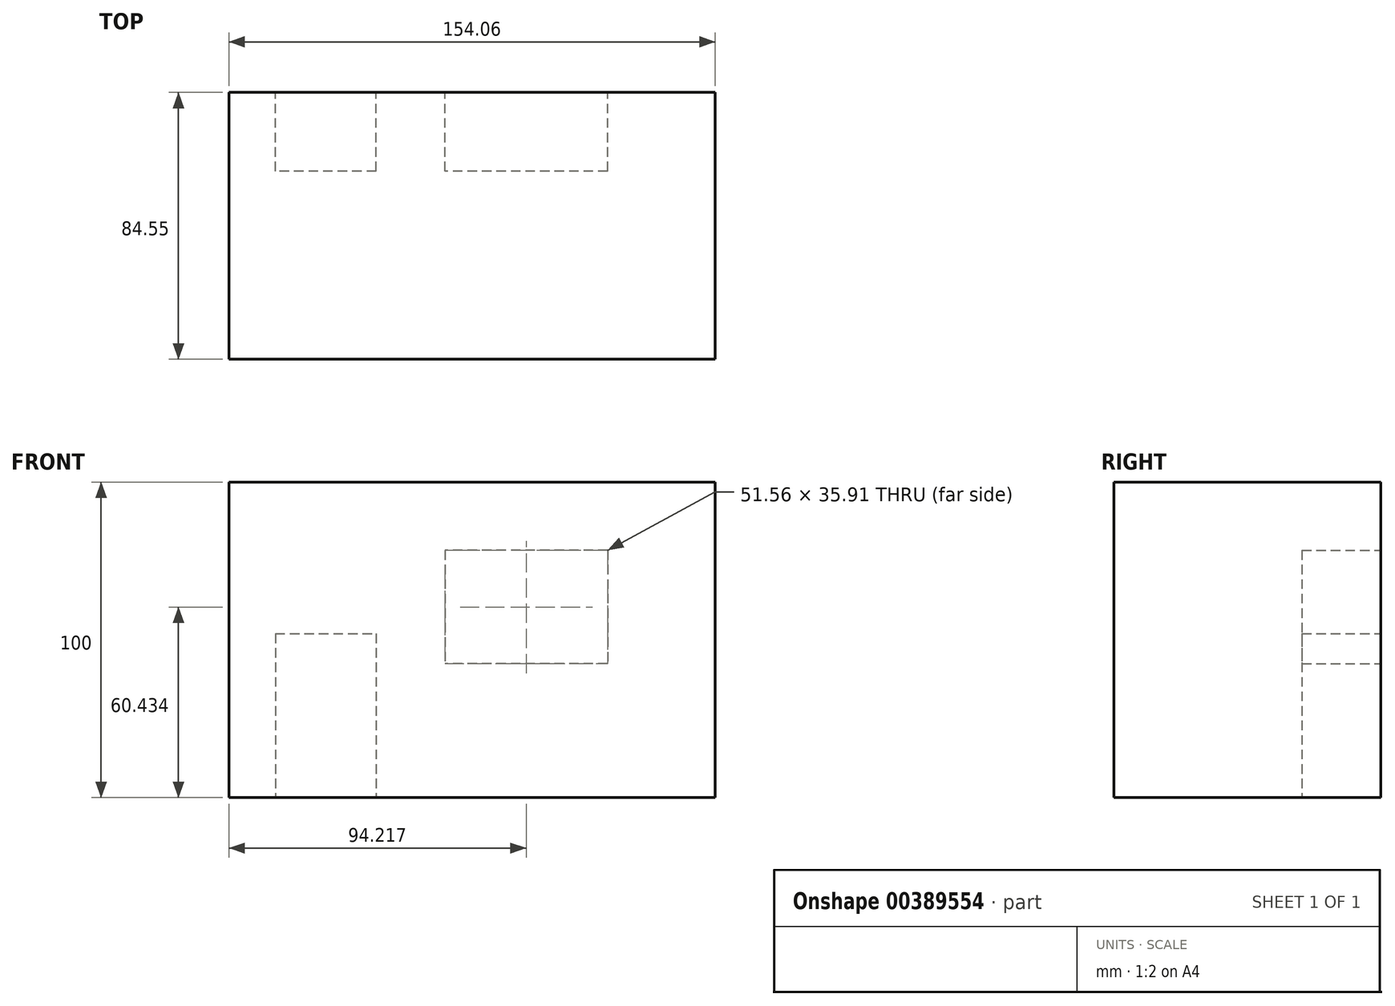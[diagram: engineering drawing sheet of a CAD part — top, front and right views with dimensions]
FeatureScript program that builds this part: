
annotation { "Feature Type Name" : "Feature", "Feature Type Description" : "" }
export const myFeature = defineFeature(function(context is Context, id is Id, definition is map)
    precondition{}
    {
        {
            var Q0;
            Q0=qCreatedBy(makeId("Top.planeOp"),FACE);
            var sketch = newSketch(context, id + "F0", { "sketchPlane" : qUnion([Q0])});
            skLineSegment(sketch, "E0.bottom", {"start": v(0, 0) * mm, "end": v(-154.06, 0) * mm});
            skLineSegment(sketch, "E0.top", {"start": v(0, -84.55) * mm, "end": v(-154.06, -84.55) * mm});
            skLineSegment(sketch, "E0.left", {"start": v(0, 0) * mm, "end": v(0, -84.55) * mm});
            skLineSegment(sketch, "E0.right", {"start": v(-154.06, 0) * mm, "end": v(-154.06, -84.55) * mm});
            skSolve(sketch);
        }
        {
            var Q0;
            Q0=makeQuery(id+"F0.imprint","IMPRINT",FACE,{"disambiguationData":[TD([[makeQuery(id+"F0.imprint","IMPRINT",EDGE,{"derivedFrom":sQuery(id+"F0.wireOp",EDGE,"E0.bottom")}),1.0]])]});
            extrude(context, id + "F1", {"entities" : qUnion([Q0]), "depth" : 100 * mm});
        }
        {
            var Q0;
            Q0=makeQuery(id+"F1.opExtrude","SWEPT_FACE",FACE,{"disambiguationData":[OSD([sQuery(id+"F0.wireOp",EDGE,"E0.bottom")])]});
            var sketch = newSketch(context, id + "F2", { "sketchPlane" : qUnion([Q0])});
            skLineSegment(sketch, "E1.bottom", {"start": v(34.06, 78.39) * mm, "end": v(85.62, 78.39) * mm});
            skLineSegment(sketch, "E1.top", {"start": v(34.06, 42.48) * mm, "end": v(85.62, 42.48) * mm});
            skLineSegment(sketch, "E1.left", {"start": v(34.06, 78.39) * mm, "end": v(34.06, 42.48) * mm});
            skLineSegment(sketch, "E1.right", {"start": v(85.62, 78.39) * mm, "end": v(85.62, 42.48) * mm});
            skLineSegment(sketch, "E2.bottom", {"start": v(139.33, 52) * mm, "end": v(107.4, 52) * mm});
            skLineSegment(sketch, "E2.top", {"start": v(139.33, -23.2) * mm, "end": v(107.4, -23.2) * mm});
            skLineSegment(sketch, "E2.left", {"start": v(139.33, 52) * mm, "end": v(139.33, -23.2) * mm});
            skLineSegment(sketch, "E2.right", {"start": v(107.4, 52) * mm, "end": v(107.4, -23.2) * mm});
            skSolve(sketch);
        }
        {
            var Q0;
            {var subQ0=sQuery(id+"F2.wireOp",EDGE,"E2.top");Q0=makeQuery(id+"F2.imprint","IMPRINT",FACE,{"disambiguationData":[TD([[makeQuery(id+"F2.imprint","IMPRINT",EDGE,{"derivedFrom":subQ0}),-1.0]])]});}
            var Q1;
            {var subQ0=sQuery(id+"F2.wireOp",EDGE,"E2.bottom");Q1=makeQuery(id+"F2.imprint","IMPRINT",FACE,{"disambiguationData":[TD([[makeQuery(id+"F2.imprint","IMPRINT",EDGE,{"derivedFrom":subQ0}),1.0]])]});}
            var Q2;
            Q2=makeQuery(id+"F2.imprint","IMPRINT",FACE,{"disambiguationData":[TD([[makeQuery(id+"F2.imprint","IMPRINT",EDGE,{"derivedFrom":sQuery(id+"F2.wireOp",EDGE,"E1.bottom")}),-1.0]])]});
            extrude(context, id + "F3", {"entities" : qUnion([Q0, Q1, Q2]), "operationType" : NewBodyOperationType.REMOVE, "oppositeDirection" : true, "depth" : 25 * mm});
        }
    });
